# Revit family: Check Valve-JCI_Sapphire_Plus-(70bar)Novec1230
name_source: partatom
category: Specialty Equipment
revit_build: Autodesk Revit 2017 (Build: 20171027_0315(x64)
units: mm (PartAtom-declared; Revit-internal decimal feet)

## family parameters
Always vertical = Yes
Cut with Voids When Loaded = No
OmniClass Number = 23.29.33.13.11
Part Type = Normal
Room Calculation Point = No
Round Connector Dimension = Use Diameter
Shared = Yes
Work Plane-Based = Yes

## types (2) — shared parameters
Assembly Code = D4090300
Date Modified = YYYY/MM/DD
Default Elevation = 1219.2 mm  [stored 4 ft]
Description = Manifold Check Valve
Equipment Abbreviation = CV
Equipment Number = XXX
Family Version = 1.0
Fire Suppression Agent = 3M™ Novec™ 1230 Fire Protection Fluid
Manufacturer = Johnson Controls, Inc.
Model Disclaimer = For More Information Contact JOHNSON CONTROLS
Part Description = Manifold Check Valve
Product Documentation Link = http://www.sapphireplus.com
Product Page URL = http://www.sapphireplus.com
URL = http://www.sapphireplus.com
zero-valued in all types: Width

## per-type parameters (varying)
| type | BG | Height | Inlet | Model | Outlet | Part Number | VH | VHW |
| 25mm | 13.12 mm | 0 mm  [stored 0 ft] | 16 mm  [stored 0.0524934 ft] | 302.209.004 | 20 mm  [stored 0.0656168 ft] | 302.209.004 | 37.27 mm | 42 mm  [stored 0.137795 ft] |
| 50mm | 16.12 mm  [stored 0.0528871 ft] | 55.46 mm  [stored 0.181955 ft] | 30 mm  [stored 0.0984252 ft] | 302.209.005 | 34 mm | 302.209.005 | 55.46 mm  [stored 0.181955 ft] | 70 mm  [stored 0.229659 ft] |

note: [stored X ft] marks values corroborated as IEEE doubles in the binary element streams (Revit-internal decimal feet)

## geometry (parser evidence)
native form markers: Sweep x2
no freeform markers — native parametric forms only
